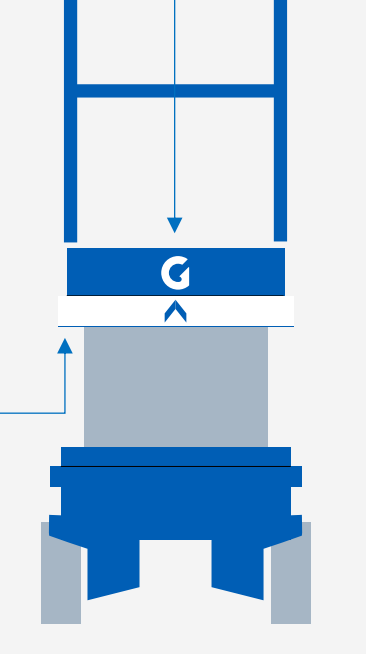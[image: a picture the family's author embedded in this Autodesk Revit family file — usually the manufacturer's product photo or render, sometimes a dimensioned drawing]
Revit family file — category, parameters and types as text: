
# Revit family: Genie_ElectricScissorLift_(GS-1932)
name_source: partatom
category: Site
units: mm (PartAtom-declared; Revit-internal decimal feet)

## family parameters
Always vertical = Yes
Cut with Voids When Loaded = No
OmniClass Number = 23.50.05.14.11
OmniClass Title = Scissors Lifts
Part Type = Normal
Round Connector Dimension = Use Diameter
Shared = No
Work Plane-Based = No

## types (1)
- GS-1932 Electric Scissor Lift
    Assembly Code = E1030900
    AssetType = Moveable
    BIMObjectName = Genie_ElectricScissorLift_(GS-1932)
    BaseHeight = 575 mm
    Blue = Steel, Paint Finish, Blue, Genie
    ClassificationName = Uniclass2015
    ClassificationValue = TE_30_30_60_60
    Clearance = ClearanceZone
    Color = Blue
    Cost = 0 $
    Description = GS-1932 Electric Scissor Lift
    DocumentationCertificates = https://www.bimstore.co
    DocumentationInstallationGuide = https://www.bimstore.co
    DocumentationLiterature = https://www.bimstore.co
    DocumentationMaintenance = https://www.bimstore.co
    DocumentationTechnical = https://www.bimstore.co
    DurationUnit = Years
    ExpectedLife = 0
    Grey = Steel, Paint Finish, Grey, Genie
    HeightStowed = 0 mm  [stored 0 ft]
    IfcExportAs = IfcTransportElement
    IfcExportType = IfcTransportElementType
    Keynote = X
    LengthStowed = 0 mm  [stored 0 ft]
    LiftCapacityMaximum = 0.00 kg
    Manufacturer = Genie
    ManufacturerName = Genie
    Model = GS-1932 Electric Scissor Lift
    ModelNumber = GS-1932
    ModelReference = Electric Scissor Lift
    NBSDescription = Scissor lifts
    NBSObjectName = Genie - Scissor lifts
    NominalDepth = 0 mm  [stored 0 ft]
    NominalHeight = 0 mm  [stored 0 ft]
    NominalLength = 0 mm  [stored 0 ft]
    ProductionYear = 2023
    ScissorPosition = 889 mm
    SpareParts = https://www.genielift.com
    Tire = Rubber, Tire, Grey
    TurningRadiusInside = 0 mm  [stored 0 ft]
    TurningRadiusOutside = 0 mm  [stored 0 ft]
    Type Comments = GS-1932 Electric Scissor Lift
    TypeName = GS-1932 Electric Scissor Lift
    URL = https://www.genielift.com
    WarrantyDurationLabor = 0
    WarrantyDurationParts = 0
    WarrantyDurationUnit = Years
    WarrantyGuarantorLabor = https://www.genielift.com
    WarrantyGuarantorParts = https://www.genielift.com
    Weight = 0.00 kg
    White = White
    Width = 0 mm  [stored 0 ft]
    _BSBibleVersion = 17
    _BimSpecGuid = 0
    _CurrentRevision = 1
    _DistributedBy = https://www.bimstore.co
    _ObjectUserGuide = https://www.bimstore.co

note: [stored X ft] marks values corroborated as IEEE doubles in the binary element streams (Revit-internal decimal feet)

## geometry (parser evidence)
native form markers: Sweep x17
no freeform markers — native parametric forms only
